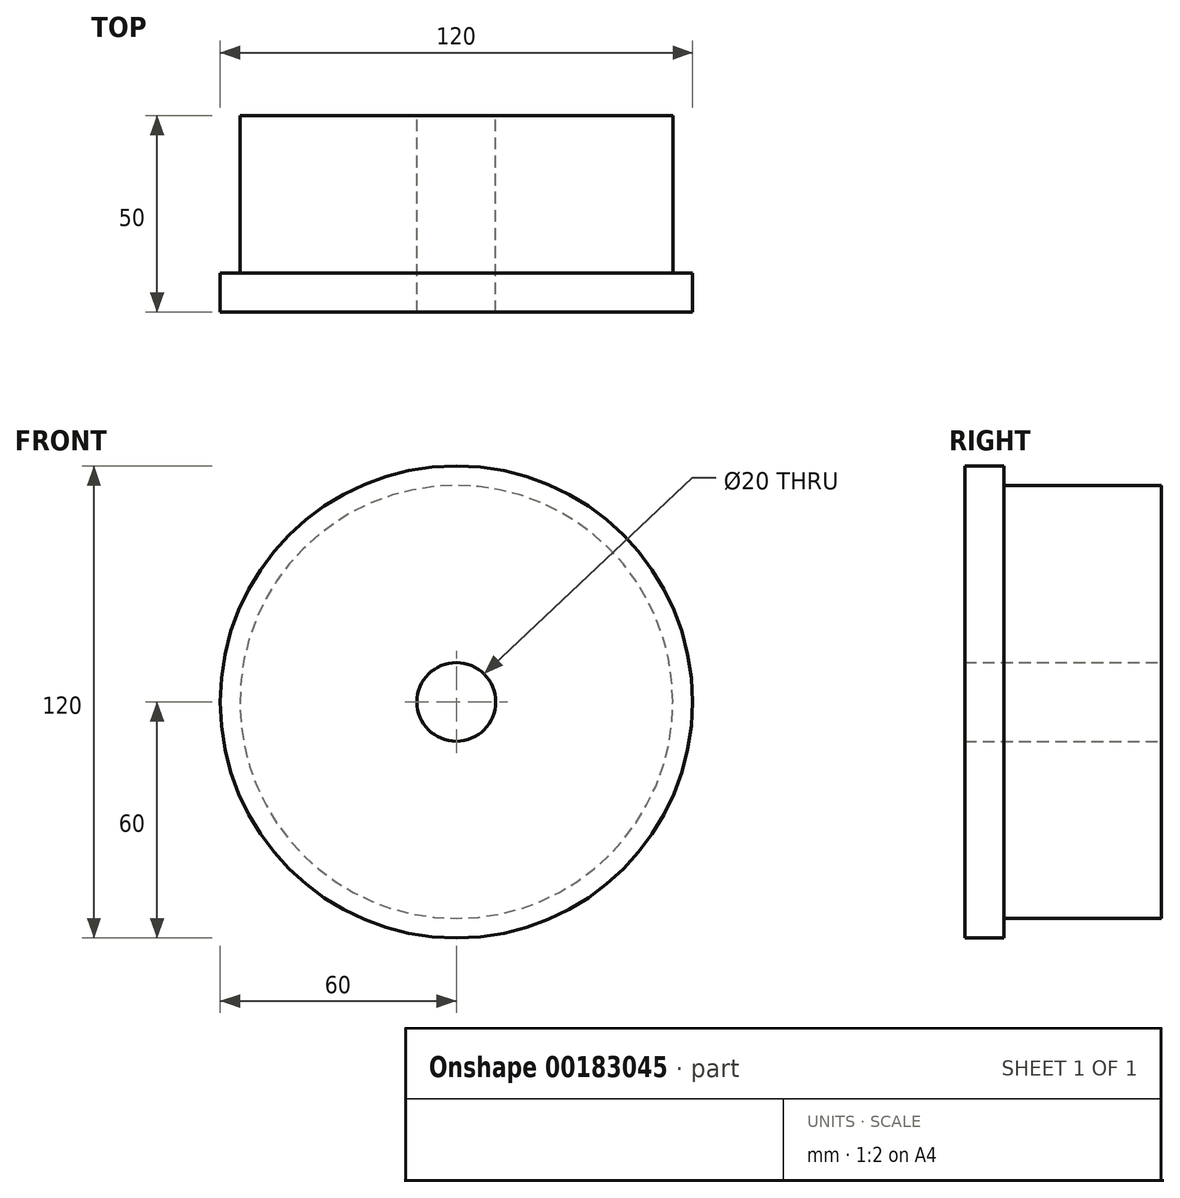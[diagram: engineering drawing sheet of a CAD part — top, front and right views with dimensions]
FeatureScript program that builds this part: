
annotation { "Feature Type Name" : "Feature", "Feature Type Description" : "" }
export const myFeature = defineFeature(function(context is Context, id is Id, definition is map)
    precondition{}
    {
        {
            var Q0;
            Q0=qCreatedBy(makeId("Right.planeOp"),FACE);
            var sketch = newSketch(context, id + "F0", { "sketchPlane" : qUnion([Q0])});
            skLineSegment(sketch, "E0", {"start": v(0, 10) * mm, "end": v(0, 60) * mm});
            skLineSegment(sketch, "E1", {"start": v(0, 60) * mm, "end": v(10, 60) * mm});
            skLineSegment(sketch, "E2", {"start": v(10, 60) * mm, "end": v(10, 55) * mm});
            skLineSegment(sketch, "E3", {"start": v(10, 55) * mm, "end": v(50, 55) * mm});
            skLineSegment(sketch, "E4", {"start": v(50, 55) * mm, "end": v(50, 10) * mm});
            skLineSegment(sketch, "E5", {"start": v(50, 10) * mm, "end": v(0, 10) * mm});
            skPoint(sketch, "E6.orphan", {"position": v(50, 0) * mm});
            skLineSegment(sketch, "E7", {"start": v(60.88, 0) * mm, "end": v(-34.04, 0) * mm, "construction": true});
            skSolve(sketch);
        }
        {
            var Q0;
            Q0=makeQuery(id+"F0.imprint","IMPRINT",FACE,{"disambiguationData":[TD([[makeQuery(id+"F0.imprint","IMPRINT",EDGE,{"derivedFrom":sQuery(id+"F0.wireOp",EDGE,"E0")}),-1.0]])]});
            var Q1;
            Q1=sQuery(id+"F0.wireOp",EDGE,"E7");
            revolve(context, id + "F1", {"entities" : qUnion([Q0]), "axis" : qUnion([Q1]), "revolveType" : RevolveType.FULL});
        }
    });
